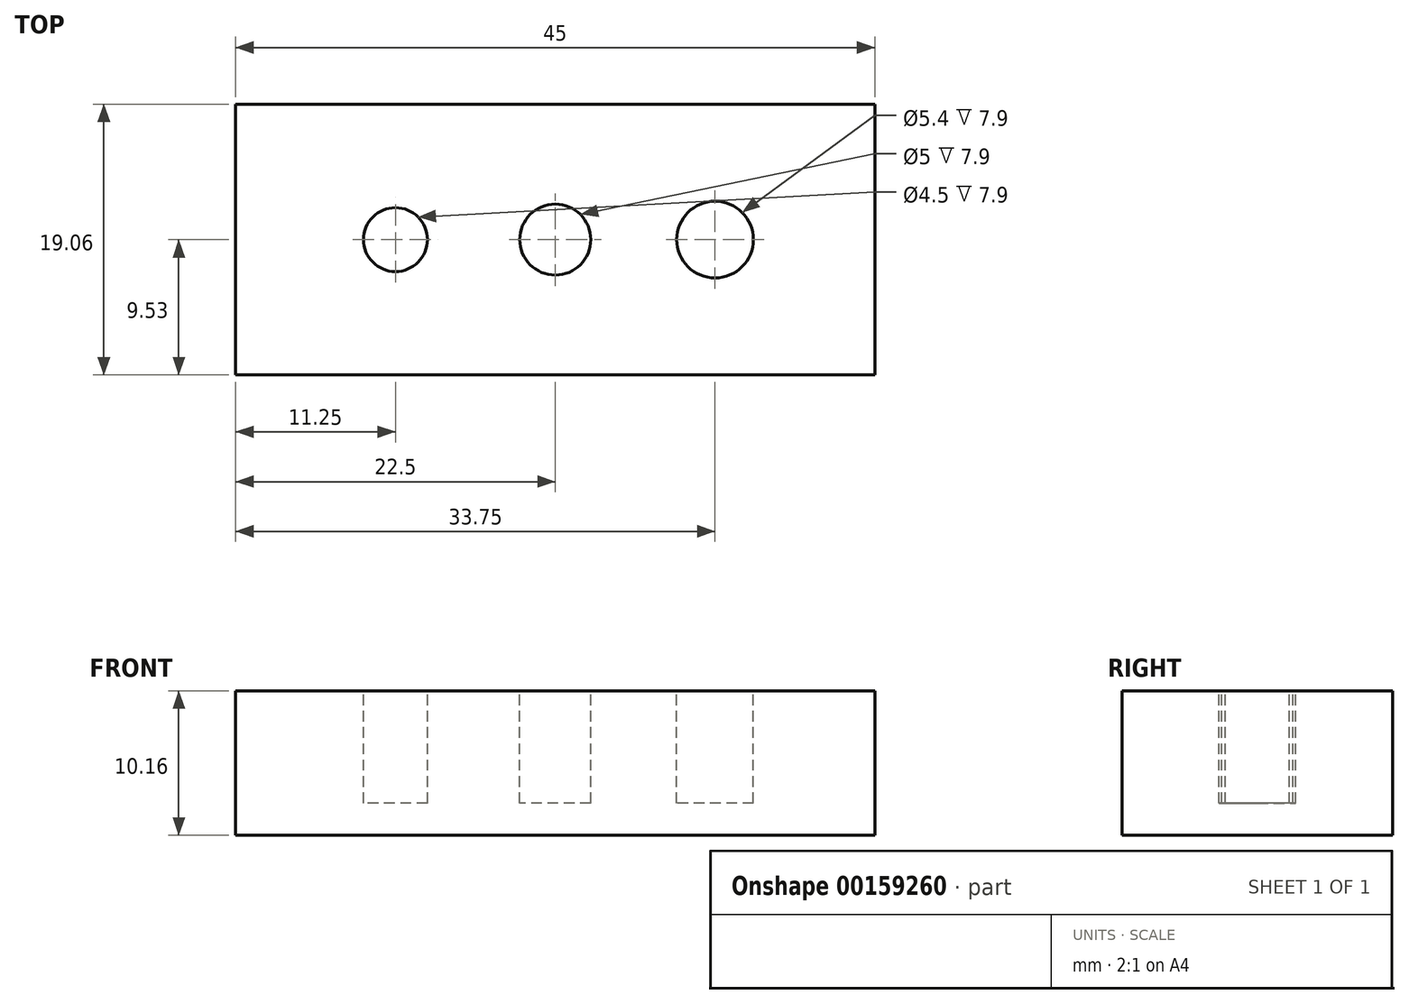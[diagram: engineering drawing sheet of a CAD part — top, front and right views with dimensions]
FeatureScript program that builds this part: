
annotation { "Feature Type Name" : "Feature", "Feature Type Description" : "" }
export const myFeature = defineFeature(function(context is Context, id is Id, definition is map)
    precondition{}
    {
        {
            var Q0;
            Q0=qCreatedBy(makeId("Top.planeOp"),FACE);
            var sketch = newSketch(context, id + "F0", { "sketchPlane" : qUnion([Q0])});
            skLineSegment(sketch, "E0.bottom", {"start": v(22.5, -9.53) * mm, "end": v(-22.5, -9.53) * mm});
            skLineSegment(sketch, "E0.top", {"start": v(22.5, 9.53) * mm, "end": v(-22.5, 9.52) * mm});
            skLineSegment(sketch, "E0.left", {"start": v(22.5, -9.53) * mm, "end": v(22.5, 9.53) * mm});
            skLineSegment(sketch, "E0.right", {"start": v(-22.5, -9.53) * mm, "end": v(-22.5, 9.52) * mm});
            skPoint(sketch, "E0.middle", {"position": v(0, 0) * mm});
            skSolve(sketch);
        }
        {
            var Q0;
            Q0=makeQuery(id+"F0.imprint","IMPRINT",FACE,{"disambiguationData":[TD([[makeQuery(id+"F0.imprint","IMPRINT",EDGE,{"derivedFrom":sQuery(id+"F0.wireOp",EDGE,"E0.bottom")}),-1.0]])]});
            extrude(context, id + "F1", {"entities" : qUnion([Q0]), "depth" : 10.16 * mm});
        }
        {
            var Q0;
            Q0=makeQuery(id+"F1.opExtrude","CAP_FACE",FACE,{"disambiguationData":[OSD([sQuery(id+"F0.wireOp",EDGE,"E0.bottom"),sQuery(id+"F0.wireOp",EDGE,"E0.top"),sQuery(id+"F0.wireOp",EDGE,"E0.left"),sQuery(id+"F0.wireOp",EDGE,"E0.right")])],"isStart":false});
            var sketch = newSketch(context, id + "F2", { "sketchPlane" : qUnion([Q0])});
            skLineSegment(sketch, "E1", {"start": v(-22.5, 0) * mm, "end": v(0, 0) * mm, "construction": true});
            skCircle(sketch, "E2", {"center": v(0, 0) * mm, "radius": 2.5 * mm});
            skCircle(sketch, "E3", {"center": v(-11.25, 0) * mm, "radius": 2.25 * mm});
            skLineSegment(sketch, "E4", {"start": v(0, 0) * mm, "end": v(22.5, 0) * mm, "construction": true});
            skCircle(sketch, "E5", {"center": v(11.25, 0) * mm, "radius": 2.7 * mm});
            skSolve(sketch);
        }
        {
            var Q0;
            Q0=makeQuery(id+"F2.imprint","IMPRINT",FACE,{"disambiguationData":[TD([[makeQuery(id+"F2.imprint","IMPRINT",EDGE,{"derivedFrom":sQuery(id+"F2.wireOp",EDGE,"E3")}),1.0]])]});
            var Q1;
            Q1=makeQuery(id+"F2.imprint","IMPRINT",FACE,{"disambiguationData":[TD([[makeQuery(id+"F2.imprint","IMPRINT",EDGE,{"derivedFrom":sQuery(id+"F2.wireOp",EDGE,"E2")}),1.0]])]});
            var Q2;
            Q2=makeQuery(id+"F2.imprint","IMPRINT",FACE,{"disambiguationData":[TD([[makeQuery(id+"F2.imprint","IMPRINT",EDGE,{"derivedFrom":sQuery(id+"F2.wireOp",EDGE,"E5")}),1.0]])]});
            extrude(context, id + "F3", {"entities" : qUnion([Q0, Q1, Q2]), "operationType" : NewBodyOperationType.REMOVE, "oppositeDirection" : true, "depth" : 7.9 * mm});
        }
    });
